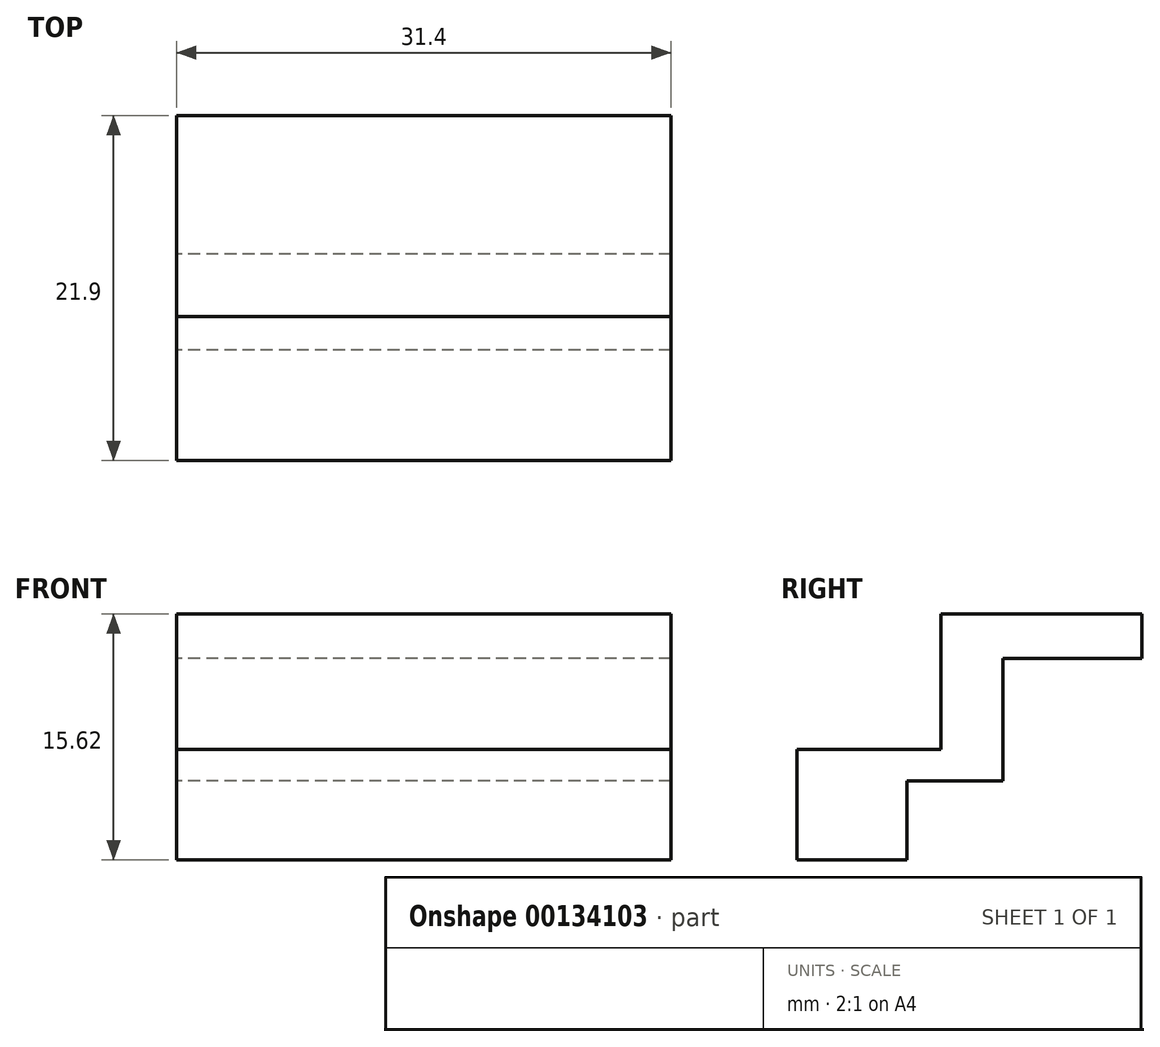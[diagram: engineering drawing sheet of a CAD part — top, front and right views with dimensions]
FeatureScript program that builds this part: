
annotation { "Feature Type Name" : "Feature", "Feature Type Description" : "" }
export const myFeature = defineFeature(function(context is Context, id is Id, definition is map)
    precondition{}
    {
        {
            var Q0;
            Q0=qCreatedBy(makeId("Right.planeOp"),FACE);
            var sketch = newSketch(context, id + "F0", { "sketchPlane" : qUnion([Q0])});
            skLineSegment(sketch, "E0", {"start": v(0, 0) * mm, "end": v(0, 7.8) * mm});
            skLineSegment(sketch, "E1", {"start": v(0, 7.8) * mm, "end": v(8.8, 7.8) * mm});
            skLineSegment(sketch, "E2", {"start": v(0, 0) * mm, "end": v(-6.1, 0) * mm});
            skLineSegment(sketch, "E3", {"start": v(8.8, 7.8) * mm, "end": v(8.8, 10.62) * mm});
            skLineSegment(sketch, "E4", {"start": v(8.8, 10.62) * mm, "end": v(-3.95, 10.62) * mm});
            skLineSegment(sketch, "E5", {"start": v(-3.95, 10.62) * mm, "end": v(-3.95, 2) * mm});
            skLineSegment(sketch, "E6", {"start": v(-3.95, 2) * mm, "end": v(-13.1, 2) * mm});
            skLineSegment(sketch, "E7", {"start": v(-13.1, 2) * mm, "end": v(-13.1, -5) * mm});
            skLineSegment(sketch, "E8", {"start": v(-13.1, -5) * mm, "end": v(-6.1, -5) * mm});
            skLineSegment(sketch, "E9", {"start": v(-6.1, -5) * mm, "end": v(-6.1, 0) * mm});
            skSolve(sketch);
        }
        {
            var Q0;
            Q0=makeQuery(id+"F0.imprint","IMPRINT",FACE,{"disambiguationData":[TD([[makeQuery(id+"F0.imprint","IMPRINT",EDGE,{"derivedFrom":sQuery(id+"F0.wireOp",EDGE,"E0")}),1.0]])]});
            extrude(context, id + "F1", {"entities" : qUnion([Q0]), "depth" : 31.4 * mm});
        }
    });
